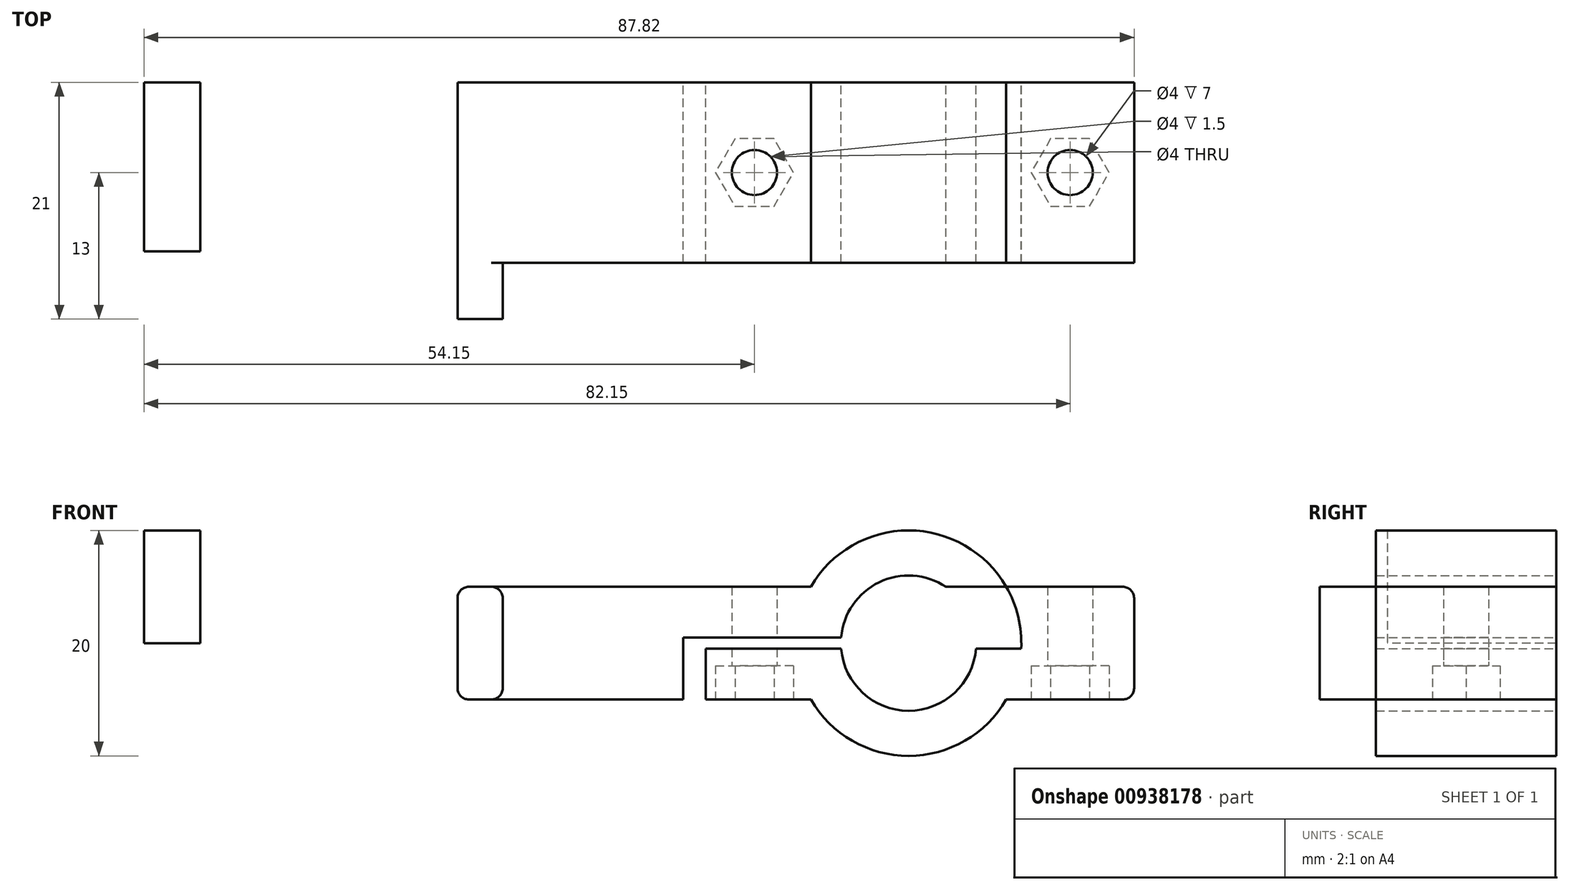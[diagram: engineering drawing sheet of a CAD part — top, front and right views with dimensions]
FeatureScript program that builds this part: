
annotation { "Feature Type Name" : "Feature", "Feature Type Description" : "" }
export const myFeature = defineFeature(function(context is Context, id is Id, definition is map)
    precondition{}
    {
        {
            var Q0;
            Q0=qCreatedBy(makeId("Front.planeOp"),FACE);
            var sketch = newSketch(context, id + "F0", { "sketchPlane" : qUnion([Q0])});
            skCircle(sketch, "E0", {"center": v(0, 0) * mm, "radius": 6 * mm});
            skCircle(sketch, "E1", {"center": v(0, 0) * mm, "radius": 10 * mm});
            skLineSegment(sketch, "E2.bottom", {"start": v(-40, 5) * mm, "end": v(20, 5) * mm});
            skLineSegment(sketch, "E2.top", {"start": v(-40, -5) * mm, "end": v(20, -5) * mm});
            skLineSegment(sketch, "E2.left", {"start": v(-40, 5) * mm, "end": v(-40, -5) * mm});
            skLineSegment(sketch, "E2.right", {"start": v(20, 5) * mm, "end": v(20, -5) * mm});
            skLineSegment(sketch, "E3.bottom", {"start": v(20, 0.5) * mm, "end": v(-20, 0.5) * mm});
            skLineSegment(sketch, "E3.top", {"start": v(20, -0.5) * mm, "end": v(-20, -0.5) * mm});
            skLineSegment(sketch, "E3.left", {"start": v(20, 0.5) * mm, "end": v(20, -0.5) * mm});
            skLineSegment(sketch, "E3.right", {"start": v(-20, 0.5) * mm, "end": v(-20, -0.5) * mm});
            skLineSegment(sketch, "E4.bottom", {"start": v(-20, 0.5) * mm, "end": v(-18, 0.5) * mm});
            skLineSegment(sketch, "E4.top", {"start": v(-20, -5) * mm, "end": v(-18, -5) * mm});
            skLineSegment(sketch, "E4.left", {"start": v(-20, 0.5) * mm, "end": v(-20, -5) * mm});
            skLineSegment(sketch, "E4.right", {"start": v(-18, 0.5) * mm, "end": v(-18, -5) * mm});
            skSolve(sketch);
        }
        {
            var Q0;
            {var subQ5=sQuery(id+"F0.wireOp",EDGE,"E2.left");Q0=makeQuery(id+"F0.imprint","IMPRINT",FACE,{"disambiguationData":[TD([[makeQuery(id+"F0.imprint","IMPRINT",EDGE,{"derivedFrom":subQ5}),1.0]])]});}
            var Q1;
            {var subQ0=sQuery(id+"F0.wireOp",EDGE,"E2.bottom");var subQ1=sQuery(id+"F0.wireOp",EDGE,"E0");var subQ2=makeQuery(id+"F0.imprint","INTERSECT",VERTEX,{"disambiguationData":[OD(0.0)],"derivedFrom":[subQ1,subQ0]});Q1=makeQuery(id+"F0.imprint","IMPRINT",FACE,{"disambiguationData":[TD([[makeQuery(id+"F0.imprint","IMPRINT",EDGE,{"disambiguationData":[TD([[subQ2,-1.0]])],"derivedFrom":subQ1}),-1.0]])]});}
            var Q2;
            {var subQ0=sQuery(id+"F0.wireOp",EDGE,"E2.bottom");var subQ1=sQuery(id+"F0.wireOp",EDGE,"E0");var subQ2=makeQuery(id+"F0.imprint","INTERSECT",VERTEX,{"disambiguationData":[OD(0.0)],"derivedFrom":[subQ1,subQ0]});Q2=makeQuery(id+"F0.imprint","IMPRINT",FACE,{"disambiguationData":[TD([[makeQuery(id+"F0.imprint","IMPRINT",EDGE,{"disambiguationData":[TD([[subQ2,1.0]])],"derivedFrom":subQ1}),-1.0]])]});}
            var Q3;
            {var subQ3=sQuery(id+"F0.wireOp",EDGE,"E2.right");Q3=makeQuery(id+"F0.imprint","IMPRINT",FACE,{"disambiguationData":[TD([[makeQuery(id+"F0.imprint","IMPRINT",EDGE,{"derivedFrom":subQ3}),-1.0]])]});}
            var Q4;
            {var subQ0=sQuery(id+"F0.wireOp",EDGE,"E2.top");var subQ1=sQuery(id+"F0.wireOp",EDGE,"E0");var subQ2=makeQuery(id+"F0.imprint","INTERSECT",VERTEX,{"disambiguationData":[OD(0.0)],"derivedFrom":[subQ1,subQ0]});Q4=makeQuery(id+"F0.imprint","IMPRINT",FACE,{"disambiguationData":[TD([[makeQuery(id+"F0.imprint","IMPRINT",EDGE,{"disambiguationData":[TD([[subQ2,1.0]])],"derivedFrom":subQ1}),-1.0]])]});}
            var Q5;
            {var subQ0=sQuery(id+"F0.wireOp",EDGE,"E2.bottom");var subQ1=sQuery(id+"F0.wireOp",EDGE,"E0");var subQ2=makeQuery(id+"F0.imprint","INTERSECT",VERTEX,{"disambiguationData":[OD(1.0)],"derivedFrom":[subQ1,subQ0]});Q5=makeQuery(id+"F0.imprint","IMPRINT",FACE,{"disambiguationData":[TD([[makeQuery(id+"F0.imprint","IMPRINT",EDGE,{"disambiguationData":[TD([[subQ2,-1.0]])],"derivedFrom":subQ1}),-1.0]])]});}
            var Q6;
            {var subQ0=sQuery(id+"F0.wireOp",EDGE,"E3.top");var subQ1=sQuery(id+"F0.wireOp",EDGE,"E0");var subQ2=makeQuery(id+"F0.imprint","INTERSECT",VERTEX,{"disambiguationData":[OD(1.0)],"derivedFrom":[subQ1,subQ0]});Q6=makeQuery(id+"F0.imprint","IMPRINT",FACE,{"disambiguationData":[TD([[makeQuery(id+"F0.imprint","IMPRINT",EDGE,{"disambiguationData":[TD([[subQ2,-1.0]])],"derivedFrom":subQ1}),-1.0]])]});}
            var Q7;
            {var subQ0=sQuery(id+"F0.wireOp",EDGE,"E2.top");var subQ1=sQuery(id+"F0.wireOp",EDGE,"E1");var subQ2=makeQuery(id+"F0.imprint","INTERSECT",VERTEX,{"disambiguationData":[OD(1.0)],"derivedFrom":[subQ1,subQ0]});Q7=makeQuery(id+"F0.imprint","IMPRINT",FACE,{"disambiguationData":[TD([[makeQuery(id+"F0.imprint","IMPRINT",EDGE,{"disambiguationData":[TD([[subQ2,1.0]])],"derivedFrom":subQ1}),-1.0]])]});}
            var Q8;
            {var subQ0=sQuery(id+"F0.wireOp",EDGE,"E3.top");var subQ1=sQuery(id+"F0.wireOp",EDGE,"E0");var subQ2=makeQuery(id+"F0.imprint","INTERSECT",VERTEX,{"disambiguationData":[OD(0.0)],"derivedFrom":[subQ1,subQ0]});Q8=makeQuery(id+"F0.imprint","IMPRINT",FACE,{"disambiguationData":[TD([[makeQuery(id+"F0.imprint","IMPRINT",EDGE,{"disambiguationData":[TD([[subQ2,1.0]])],"derivedFrom":subQ1}),-1.0]])]});}
            extrude(context, id + "F1", {"entities" : qUnion([Q0, Q1, Q2, Q3, Q4, Q5, Q6, Q7, Q8]), "depth" : 16 * mm, "offsetDistance" : 25 * mm});
        }
        {
            var Q0;
            Q0=makeQuery(id+"F1.opExtrude","CAP_FACE",FACE,{"disambiguationData":[OSD([sQuery(id+"F0.wireOp",EDGE,"E0"),sQuery(id+"F0.wireOp",EDGE,"E1"),sQuery(id+"F0.wireOp",EDGE,"E2.bottom"),sQuery(id+"F0.wireOp",EDGE,"E2.top"),sQuery(id+"F0.wireOp",EDGE,"E2.left"),sQuery(id+"F0.wireOp",EDGE,"E2.right"),sQuery(id+"F0.wireOp",EDGE,"E3.bottom"),sQuery(id+"F0.wireOp",EDGE,"E3.right"),sQuery(id+"F0.wireOp",EDGE,"E4.left")])],"isStart":false});
            var sketch = newSketch(context, id + "F2", { "sketchPlane" : qUnion([Q0])});
            skLineSegment(sketch, "E5.bottom", {"start": v(-40, 5) * mm, "end": v(-36, 5) * mm});
            skLineSegment(sketch, "E5.top", {"start": v(-40, -5) * mm, "end": v(-36, -5) * mm});
            skLineSegment(sketch, "E5.left", {"start": v(-40, 5) * mm, "end": v(-40, -5) * mm});
            skLineSegment(sketch, "E5.right", {"start": v(-36, 5) * mm, "end": v(-36, -5) * mm});
            skSolve(sketch);
        }
        {
            var Q0;
            Q0=makeQuery(id+"F2.imprint","IMPRINT",FACE,{"disambiguationData":[TD([[makeQuery(id+"F2.imprint","IMPRINT",EDGE,{"derivedFrom":sQuery(id+"F2.wireOp",EDGE,"E5.bottom")}),-1.0]])]});
            extrude(context, id + "F3", {"entities" : qUnion([Q0]), "operationType" : NewBodyOperationType.ADD, "depth" : 5 * mm, "offsetDistance" : 25 * mm});
        }
        {
            var Q0;
            {var subQ0=sQuery(id+"F0.wireOp",EDGE,"E2.top");Q0=makeQuery(id+"F1.opExtrude","SWEPT_FACE",FACE,{"disambiguationData":[OSD([subQ0]),TDD([makeQuery(id+"F0.imprint","IMPRINT",EDGE,{"disambiguationData":[TD([[makeQuery(id+"F0.imprint","INTERSECT",VERTEX,{"derivedFrom":[subQ0,sQuery(id+"F0.wireOp",EDGE,"E2.right")]}),1.0]])],"derivedFrom":subQ0})])]});}
            var sketch = newSketch(context, id + "F4", { "sketchPlane" : qUnion([Q0])});
            skCircle(sketch, "E6", {"center": v(14.33, 8) * mm, "radius": 2 * mm});
            skPoint(sketch, "E6.centerSnap0", {"position": v(14.33, 0) * mm});
            skPoint(sketch, "E6.centerSnap1", {"position": v(20, 8) * mm});
            skCircle(sketch, "E7", {"center": v(-13.67, 8) * mm, "radius": 2 * mm});
            skSolve(sketch);
        }
        {
            var Q0;
            Q0=makeQuery(id+"F4.imprint","IMPRINT",FACE,{"disambiguationData":[TD([[makeQuery(id+"F4.imprint","IMPRINT",EDGE,{"derivedFrom":sQuery(id+"F4.wireOp",EDGE,"E7")}),1.0]])]});
            var Q1;
            Q1=makeQuery(id+"F4.imprint","IMPRINT",FACE,{"disambiguationData":[TD([[makeQuery(id+"F4.imprint","IMPRINT",EDGE,{"derivedFrom":sQuery(id+"F4.wireOp",EDGE,"E6")}),1.0]])]});
            extrude(context, id + "F5", {"entities" : qUnion([Q0, Q1]), "operationType" : NewBodyOperationType.REMOVE, "oppositeDirection" : true, "depth" : 25 * mm, "offsetDistance" : 25 * mm});
        }
        {
            var Q0;
            {var subQ0=sQuery(id+"F0.wireOp",EDGE,"E2.top");Q0=makeQuery(id+"F1.opExtrude","SWEPT_FACE",FACE,{"disambiguationData":[OSD([subQ0]),TDD([makeQuery(id+"F0.imprint","IMPRINT",EDGE,{"disambiguationData":[TD([[makeQuery(id+"F0.imprint","INTERSECT",VERTEX,{"derivedFrom":[subQ0,sQuery(id+"F0.wireOp",EDGE,"E4.right")]}),-1.0]])],"derivedFrom":subQ0})])]});}
            var sketch = newSketch(context, id + "F6", { "sketchPlane" : qUnion([Q0])});
            skCircle(sketch, "E8.cCircle", {"center": v(-13.67, 8) * mm, "radius": 3 * mm, "construction": true});
            skLineSegment(sketch, "E8.0", {"start": v(-11.94, 5) * mm, "end": v(-15.4, 5) * mm});
            skLineSegment(sketch, "E8.1", {"start": v(-15.4, 5) * mm, "end": v(-17.13, 8) * mm});
            skLineSegment(sketch, "E8.2", {"start": v(-17.13, 8) * mm, "end": v(-15.4, 11) * mm});
            skLineSegment(sketch, "E8.3", {"start": v(-15.4, 11) * mm, "end": v(-11.94, 11) * mm});
            skLineSegment(sketch, "E8.4", {"start": v(-11.94, 11) * mm, "end": v(-10.2, 8) * mm});
            skLineSegment(sketch, "E8.5", {"start": v(-10.2, 8) * mm, "end": v(-11.94, 5) * mm});
            skPoint(sketch, "E8.0.midPoint", {"position": v(-13.67, 5) * mm});
            skCircle(sketch, "E9.cCircle", {"center": v(14.33, 8) * mm, "radius": 3 * mm, "construction": true});
            skLineSegment(sketch, "E9.0", {"start": v(16.06, 5) * mm, "end": v(12.6, 5) * mm});
            skLineSegment(sketch, "E9.1", {"start": v(12.6, 5) * mm, "end": v(10.87, 8) * mm});
            skLineSegment(sketch, "E9.2", {"start": v(10.87, 8) * mm, "end": v(12.6, 11) * mm});
            skLineSegment(sketch, "E9.3", {"start": v(12.6, 11) * mm, "end": v(16.06, 11) * mm});
            skLineSegment(sketch, "E9.4", {"start": v(16.06, 11) * mm, "end": v(17.8, 8) * mm});
            skLineSegment(sketch, "E9.5", {"start": v(17.8, 8) * mm, "end": v(16.06, 5) * mm});
            skPoint(sketch, "E9.0.midPoint", {"position": v(14.33, 5) * mm});
            skCircle(sketch, "E10.0", {"center": v(14.33, 8) * mm, "radius": 2 * mm});
            skSolve(sketch);
        }
        {
            var Q0;
            Q0=makeQuery(id+"F6.imprint","IMPRINT",FACE,{"disambiguationData":[TD([[makeQuery(id+"F6.imprint","IMPRINT",EDGE,{"derivedFrom":sQuery(id+"F6.wireOp",EDGE,"E8.0")}),-1.0]])]});
            var Q1;
            Q1=makeQuery(id+"F6.imprint","IMPRINT",FACE,{"disambiguationData":[TD([[makeQuery(id+"F6.imprint","IMPRINT",EDGE,{"derivedFrom":sQuery(id+"F6.wireOp",EDGE,"E9.0")}),-1.0]])]});
            extrude(context, id + "F7", {"entities" : qUnion([Q0, Q1]), "operationType" : NewBodyOperationType.REMOVE, "oppositeDirection" : true, "depth" : 3 * mm, "offsetDistance" : 25 * mm});
        }
        {
            var Q0;
            Q0=makeQuery(id+"F1.opExtrude","SWEPT_EDGE",EDGE,{"disambiguationData":[OSD([sQuery(id+"F0.wireOp",EDGE,"E2.top"),sQuery(id+"F0.wireOp",EDGE,"E2.right")])]});
            var Q1;
            Q1=makeQuery(id+"F1.opExtrude","SWEPT_EDGE",EDGE,{"disambiguationData":[OSD([sQuery(id+"F0.wireOp",EDGE,"E2.bottom"),sQuery(id+"F0.wireOp",EDGE,"E2.right")])]});
            var Q2;
            Q2=makeQuery(id+"F3.boolean.opBoolean","MERGE",EDGE,{"derivedFrom":[makeQuery(id+"F1.opExtrude","SWEPT_EDGE",EDGE,{"disambiguationData":[OSD([sQuery(id+"F0.wireOp",EDGE,"E2.top"),sQuery(id+"F0.wireOp",EDGE,"E2.left")])]}),makeQuery(id+"F3.opExtrude","SWEPT_EDGE",EDGE,{"disambiguationData":[OSD([sQuery(id+"F2.wireOp",EDGE,"E5.top"),sQuery(id+"F2.wireOp",EDGE,"E5.left")])]})]});
            var Q3;
            Q3=makeQuery(id+"F3.boolean.opBoolean","MERGE",EDGE,{"derivedFrom":[makeQuery(id+"F1.opExtrude","SWEPT_EDGE",EDGE,{"disambiguationData":[OSD([sQuery(id+"F0.wireOp",EDGE,"E2.bottom"),sQuery(id+"F0.wireOp",EDGE,"E2.left")])]}),makeQuery(id+"F3.opExtrude","SWEPT_EDGE",EDGE,{"disambiguationData":[OSD([sQuery(id+"F2.wireOp",EDGE,"E5.bottom"),sQuery(id+"F2.wireOp",EDGE,"E5.left")])]})]});
            var Q4;
            Q4=makeQuery(id+"F3.opExtrude","SWEPT_EDGE",EDGE,{"disambiguationData":[OSD([sQuery(id+"F0.wireOp",EDGE,"E2.top"),sQuery(id+"F2.wireOp",EDGE,"E5.top"),sQuery(id+"F2.wireOp",EDGE,"E5.right")])]});
            var Q5;
            Q5=makeQuery(id+"F3.opExtrude","SWEPT_EDGE",EDGE,{"disambiguationData":[OSD([sQuery(id+"F0.wireOp",EDGE,"E2.bottom"),sQuery(id+"F2.wireOp",EDGE,"E5.bottom"),sQuery(id+"F2.wireOp",EDGE,"E5.right")])]});
            fillet(context, id + "F8", {"entities" : qUnion([Q0, Q1, Q2, Q3, Q4, Q5]), "tangentPropagation" : true, "radius" : 1 * mm, "defaultsChanged" : false, "vertexSettings" : [], "allowEdgeOverflow" : false});
        }
        {
            var Q0;
            Q0=qCreatedBy(makeId("Top.planeOp"),FACE);
            var sketch = newSketch(context, id + "F9", { "sketchPlane" : qUnion([Q0])});
            skLineSegment(sketch, "E11.bottom", {"start": v(-67.82, 0) * mm, "end": v(-62.82, 0) * mm});
            skLineSegment(sketch, "E11.top", {"start": v(-67.82, -15) * mm, "end": v(-62.82, -15) * mm});
            skLineSegment(sketch, "E11.left", {"start": v(-67.82, 0) * mm, "end": v(-67.82, -15) * mm});
            skLineSegment(sketch, "E11.right", {"start": v(-62.82, 0) * mm, "end": v(-62.82, -15) * mm});
            skSolve(sketch);
        }
        {
            var Q0;
            Q0=makeQuery(id+"F9.imprint","IMPRINT",FACE,{"disambiguationData":[TD([[makeQuery(id+"F9.imprint","IMPRINT",EDGE,{"derivedFrom":sQuery(id+"F9.wireOp",EDGE,"E11.bottom")}),-1.0]])]});
            extrude(context, id + "F10", {"entities" : qUnion([Q0]), "depth" : 10 * mm, "offsetDistance" : 25 * mm});
        }
    });
